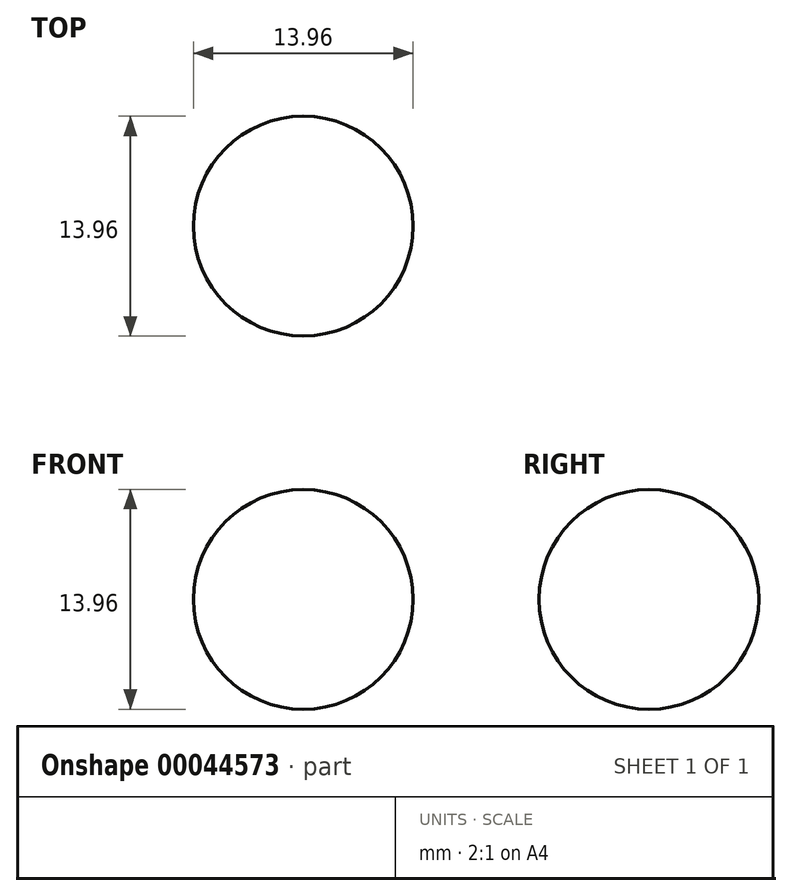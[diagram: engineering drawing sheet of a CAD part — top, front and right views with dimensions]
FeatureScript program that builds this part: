
annotation { "Feature Type Name" : "Feature", "Feature Type Description" : "" }
export const myFeature = defineFeature(function(context is Context, id is Id, definition is map)
    precondition{}
    {
        {
            var Q0;
            Q0=qCreatedBy(makeId("Top.planeOp"),FACE);
            var sketch = newSketch(context, id + "F0", { "sketchPlane" : qUnion([Q0])});
            skArc(sketch, "E0", {"start": v(6.98, 0) * mm, "mid": v(0, 6.98) * mm, "end": v(-6.98, 0) * mm});
            skLineSegment(sketch, "E1", {"start": v(6.98, 0) * mm, "end": v(-6.98, 0) * mm});
            skSolve(sketch);
        }
        {
            var Q0;
            Q0=makeQuery(id+"F0.imprint","IMPRINT",FACE,{"disambiguationData":[TD([[makeQuery(id+"F0.imprint","IMPRINT",EDGE,{"derivedFrom":sQuery(id+"F0.wireOp",EDGE,"E0")}),1.0]])]});
            var Q1;
            Q1=sQuery(id+"F0.wireOp",EDGE,"E1");
            revolve(context, id + "F1", {"entities" : qUnion([Q0]), "axis" : qUnion([Q1]), "revolveType" : RevolveType.FULL, "oppositeDirection" : true});
        }
    });
